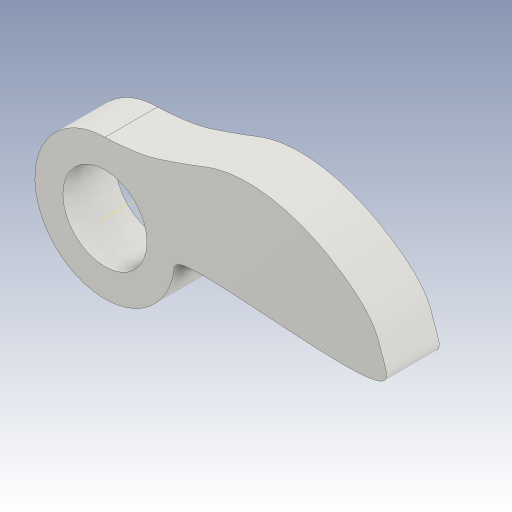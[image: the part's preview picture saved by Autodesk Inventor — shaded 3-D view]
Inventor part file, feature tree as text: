
AUTODESK INVENTOR PART (.ipt)
format: ipt  version: 2023.3 (Build 273359000, 359)  size: 121,344 bytes
history: native  units: mm (DEFAULTED — no unit token found)
features: extrude x1, hole x1, other x1, sketch x1
ambient origin geometry x8: Origin, YZ Plane, XZ Plane, XY Plane, X Axis, Y Axis, Z Axis, Center Point
bodies: Solid1 (feature_tree)
feature tree (4):
  extrude  "Nocken"  TaperAngle=0.0deg  [1 undecoded]
  hole  "Bohrung1"  [1 undecoded]
  other  "Hauptskizze"
  sketch  "Skizze2"  dims[d1=0.0mm d2=0.0mm d3=0.0mm d4=4.8mm d5=6.0mm d6=4.0mm d7=2.0mm d8=90.0deg d9=8.8mm d10=0.0mm]
note: 2 required parameter values undecoded (feature->parameter linkage not recoverable at this tier; creation-order binding heuristic only, values carry confidence <= 0.55)
